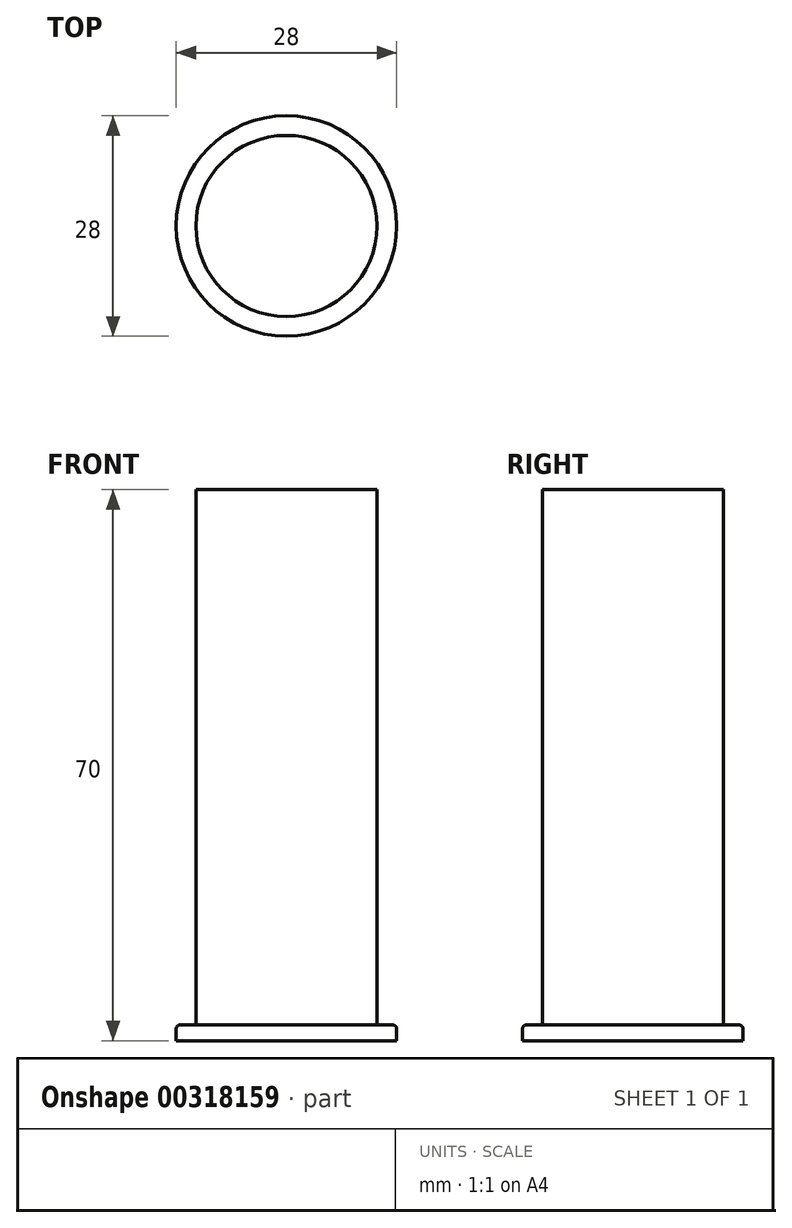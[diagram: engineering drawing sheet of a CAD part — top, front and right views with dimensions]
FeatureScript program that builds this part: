
annotation { "Feature Type Name" : "Feature", "Feature Type Description" : "" }
export const myFeature = defineFeature(function(context is Context, id is Id, definition is map)
    precondition{}
    {
        {
            var Q0;
            Q0=qCreatedBy(makeId("Top.planeOp"),FACE);
            var sketch = newSketch(context, id + "F0", { "sketchPlane" : qUnion([Q0])});
            skCircle(sketch, "E0", {"center": v(0, 0) * mm, "radius": 11.5 * mm});
            skCircle(sketch, "E1", {"center": v(0, 0) * mm, "radius": 14 * mm});
            skSolve(sketch);
        }
        {
            var Q0;
            Q0=makeQuery(id+"F0.imprint","IMPRINT",FACE,{"disambiguationData":[TD([[makeQuery(id+"F0.imprint","IMPRINT",EDGE,{"derivedFrom":sQuery(id+"F0.wireOp",EDGE,"E0")}),1.0]])]});
            extrude(context, id + "F1", {"entities" : qUnion([Q0]), "depth" : 70 * mm});
        }
        {
            var Q0;
            Q0=makeQuery(id+"F0.imprint","IMPRINT",FACE,{"disambiguationData":[TD([[makeQuery(id+"F0.imprint","IMPRINT",EDGE,{"derivedFrom":sQuery(id+"F0.wireOp",EDGE,"E0")}),-1.0]])]});
            extrude(context, id + "F2", {"entities" : qUnion([Q0]), "operationType" : NewBodyOperationType.ADD, "depth" : 2 * mm});
        }
        {
            var Q0;
            Q0=makeQuery(id+"F2.opExtrude","CAP_EDGE",EDGE,{"disambiguationData":[OSD([sQuery(id+"F0.wireOp",EDGE,"E1")])],"isStart":false});
            fillet(context, id + "F3", {"entities" : qUnion([Q0]), "radius" : .5 * mm, "tangentPropagation" : true, "allowEdgeOverflow" : false});
        }
    });
